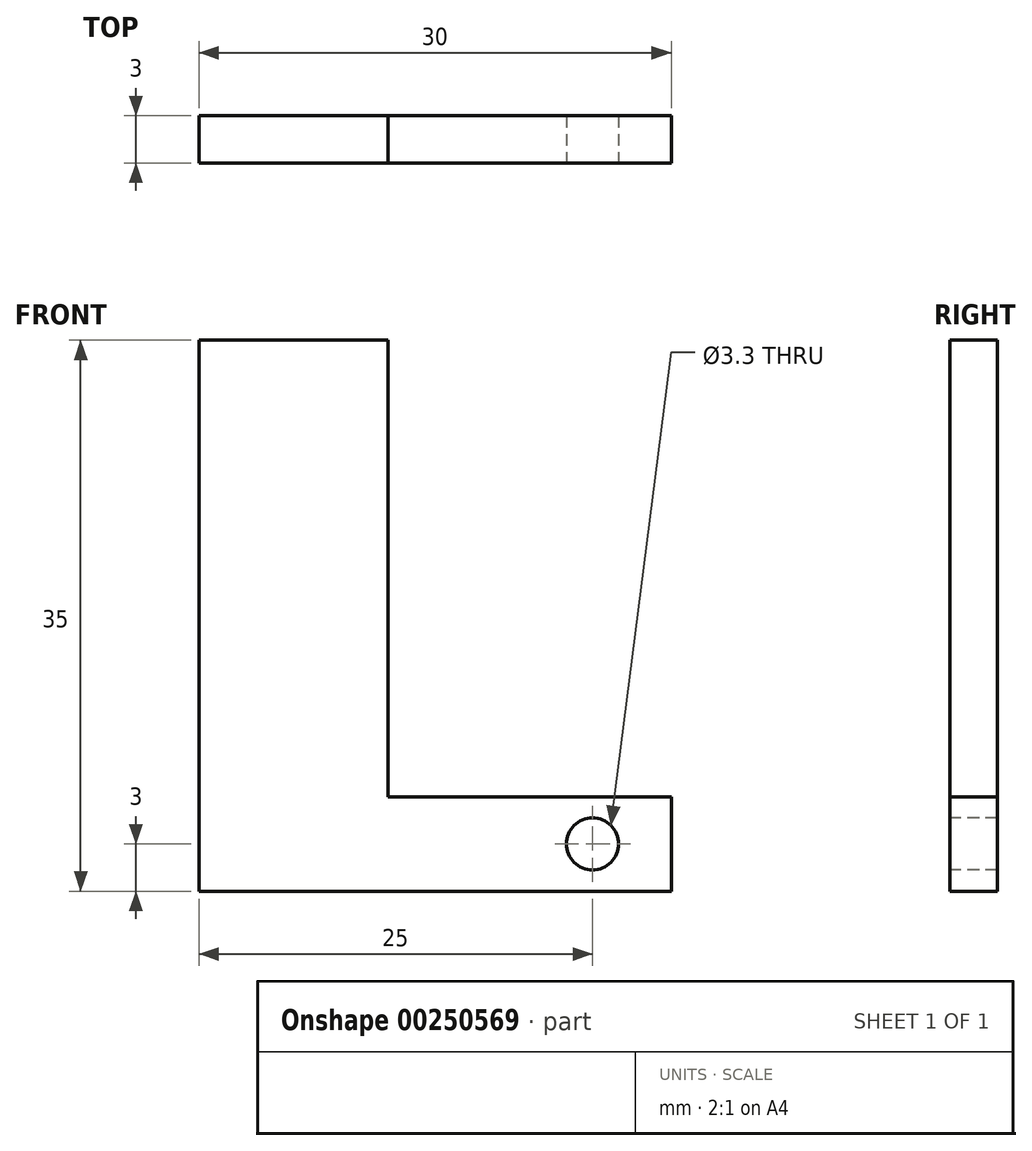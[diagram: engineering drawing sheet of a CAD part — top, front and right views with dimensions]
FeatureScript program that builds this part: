
annotation { "Feature Type Name" : "Feature", "Feature Type Description" : "" }
export const myFeature = defineFeature(function(context is Context, id is Id, definition is map)
    precondition{}
    {
        {
            var Q0;
            Q0=qCreatedBy(makeId("Front.planeOp"),FACE);
            var sketch = newSketch(context, id + "F0", { "sketchPlane" : qUnion([Q0])});
            skLineSegment(sketch, "E0.bottom", {"start": v(0, 0) * mm, "end": v(-12, 0) * mm});
            skLineSegment(sketch, "E0.top", {"start": v(0, 35) * mm, "end": v(-12, 35) * mm});
            skLineSegment(sketch, "E0.left", {"start": v(0, 0) * mm, "end": v(0, 35) * mm});
            skLineSegment(sketch, "E0.right", {"start": v(-12, 0) * mm, "end": v(-12, 35) * mm});
            skLineSegment(sketch, "E1.bottom", {"start": v(0, 0) * mm, "end": v(18, 0) * mm});
            skLineSegment(sketch, "E1.top", {"start": v(0, 6) * mm, "end": v(18, 6) * mm});
            skLineSegment(sketch, "E1.left", {"start": v(0, 0) * mm, "end": v(0, 6) * mm});
            skLineSegment(sketch, "E1.right", {"start": v(18, 0) * mm, "end": v(18, 6) * mm});
            skSolve(sketch);
        }
        {
            var Q0;
            Q0=makeQuery(id+"F0.imprint","IMPRINT",FACE,{"disambiguationData":[TD([[makeQuery(id+"F0.imprint","IMPRINT",EDGE,{"derivedFrom":sQuery(id+"F0.wireOp",EDGE,"E1.bottom")}),1.0]])]});
            var Q1;
            Q1=makeQuery(id+"F0.imprint","IMPRINT",FACE,{"disambiguationData":[TD([[makeQuery(id+"F0.imprint","IMPRINT",EDGE,{"derivedFrom":sQuery(id+"F0.wireOp",EDGE,"E0.bottom")}),-1.0]])]});
            extrude(context, id + "F1", {"entities" : qUnion([Q0, Q1]), "depth" : 3 * mm});
        }
        {
            var Q0;
            Q0=makeQuery(id+"F1.opExtrude","CAP_FACE",FACE,{"disambiguationData":[OSD([sQuery(id+"F0.wireOp",EDGE,"E0.bottom"),sQuery(id+"F0.wireOp",EDGE,"E0.top"),sQuery(id+"F0.wireOp",EDGE,"E0.left"),sQuery(id+"F0.wireOp",EDGE,"E0.right"),sQuery(id+"F0.wireOp",EDGE,"E1.bottom"),sQuery(id+"F0.wireOp",EDGE,"E1.top"),sQuery(id+"F0.wireOp",EDGE,"E1.right")])],"isStart":false});
            var sketch = newSketch(context, id + "F2", { "sketchPlane" : qUnion([Q0])});
            skPoint(sketch, "E2", {"position": v(13, 3) * mm});
            skPoint(sketch, "E2.positionSnap0", {"position": v(18, 3) * mm});
            skSolve(sketch);
        }
        {
            var Q0;
            Q0=sQuery(id+"F2.wireOp",VERTEX,"E2");
            var Q1;
            Q1=makeQuery(id+"F1.opExtrude","SWEPT_BODY",BODY,{"disambiguationData":[OSD([sQuery(id+"F0.wireOp",EDGE,"E0.bottom"),sQuery(id+"F0.wireOp",EDGE,"E0.top"),sQuery(id+"F0.wireOp",EDGE,"E0.left"),sQuery(id+"F0.wireOp",EDGE,"E0.right"),sQuery(id+"F0.wireOp",EDGE,"E1.bottom"),sQuery(id+"F0.wireOp",EDGE,"E1.top"),sQuery(id+"F0.wireOp",EDGE,"E1.right")])]});
            hole(context, id + "F3", {"style" : HoleStyle.SIMPLE, "endStyle" : HoleEndStyle.THROUGH, "holeDiameter" : 3.3 * mm, "tappedDepth" : 12 * mm, "tapClearance" : 3, "locations" : qUnion([Q0]), "scope" : qUnion([Q1])});
        }
    });
